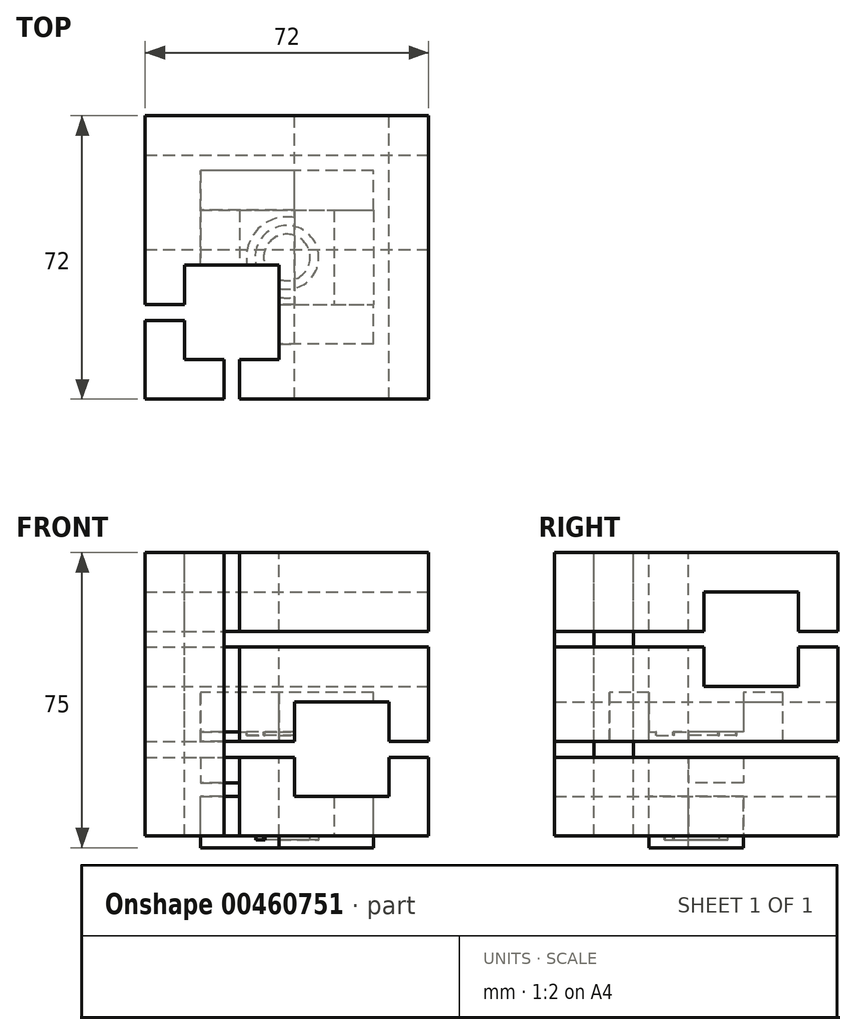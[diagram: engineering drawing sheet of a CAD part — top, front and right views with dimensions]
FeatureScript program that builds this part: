
annotation { "Feature Type Name" : "Feature", "Feature Type Description" : "" }
export const myFeature = defineFeature(function(context is Context, id is Id, definition is map)
    precondition{}
    {
        {
            var Q0;
            Q0=qCreatedBy(makeId("Top.planeOp"),FACE);
            var sketch = newSketch(context, id + "F0", { "sketchPlane" : qUnion([Q0])});
            skLineSegment(sketch, "E0.bottom", {"start": v(12, 12) * mm, "end": v(-12, 12) * mm});
            skLineSegment(sketch, "E0.top", {"start": v(12, -12) * mm, "end": v(-12, -12) * mm});
            skLineSegment(sketch, "E0.left", {"start": v(12, 12) * mm, "end": v(12, -12) * mm});
            skLineSegment(sketch, "E0.right", {"start": v(-12, 12) * mm, "end": v(-12, -12) * mm});
            skPoint(sketch, "E0.middle", {"position": v(0, 0) * mm});
            skLineSegment(sketch, "E1.bottom", {"start": v(12, 12) * mm, "end": v(22, 12) * mm});
            skLineSegment(sketch, "E1.top", {"start": v(12, -12) * mm, "end": v(22, -12) * mm});
            skLineSegment(sketch, "E1.right", {"start": v(22, 12) * mm, "end": v(22, -12) * mm});
            skLineSegment(sketch, "E2.MirrorCS", {"start": v(-12, -12) * mm, "end": v(-22, -12) * mm});
            skLineSegment(sketch, "E3.MirrorCS", {"start": v(-22, 12) * mm, "end": v(-22, -12) * mm});
            skLineSegment(sketch, "E4.MirrorCS", {"start": v(-12, 12) * mm, "end": v(-22, 12) * mm});
            skPoint(sketch, "E5", {"position": v(-17, 0) * mm});
            skPoint(sketch, "E5.positionSnap0", {"position": v(-17, 12) * mm});
            skPoint(sketch, "E5.positionSnap1", {"position": v(-22, 0) * mm});
            skPoint(sketch, "E6", {"position": v(17, 0) * mm});
            skPoint(sketch, "E6.positionSnap0", {"position": v(22, 0) * mm});
            skPoint(sketch, "E6.positionSnap1", {"position": v(17, 12) * mm});
            skCircle(sketch, "E7", {"center": v(0, 0) * mm, "radius": 8.1 * mm});
            skCircle(sketch, "E8", {"center": v(0, 0) * mm, "radius": 5.9 * mm});
            skSolve(sketch);
        }
        {
            var Q0;
            Q0=makeQuery(id+"F0.imprint","IMPRINT",FACE,{"disambiguationData":[TD([[makeQuery(id+"F0.imprint","IMPRINT",EDGE,{"derivedFrom":sQuery(id+"F0.wireOp",EDGE,"E1.bottom")}),-1.0]])]});
            var Q1;
            Q1=makeQuery(id+"F0.imprint","IMPRINT",FACE,{"disambiguationData":[TD([[makeQuery(id+"F0.imprint","IMPRINT",EDGE,{"derivedFrom":sQuery(id+"F0.wireOp",EDGE,"E0.bottom")}),1.0]])]});
            var Q2;
            Q2=makeQuery(id+"F0.imprint","IMPRINT",FACE,{"disambiguationData":[TD([[makeQuery(id+"F0.imprint","IMPRINT",EDGE,{"derivedFrom":sQuery(id+"F0.wireOp",EDGE,"E0.right")}),-1.0]])]});
            var Q3;
            Q3=makeQuery(id+"F0.imprint","IMPRINT",FACE,{"disambiguationData":[TD([[makeQuery(id+"F0.imprint","IMPRINT",EDGE,{"derivedFrom":sQuery(id+"F0.wireOp",EDGE,"E7")}),1.0]])]});
            var Q4;
            Q4=makeQuery(id+"F0.imprint","IMPRINT",FACE,{"disambiguationData":[TD([[makeQuery(id+"F0.imprint","IMPRINT",EDGE,{"derivedFrom":sQuery(id+"F0.wireOp",EDGE,"E8")}),1.0]])]});
            extrude(context, id + "F1", {"entities" : qUnion([Q0, Q1, Q2, Q3, Q4]), "oppositeDirection" : true, "depth" : 3 * mm});
        }
        {
            var Q0;
            Q0=makeQuery(id+"F0.imprint","IMPRINT",FACE,{"disambiguationData":[TD([[makeQuery(id+"F0.imprint","IMPRINT",EDGE,{"derivedFrom":sQuery(id+"F0.wireOp",EDGE,"E1.bottom")}),-1.0]])]});
            var Q1;
            Q1=makeQuery(id+"F0.imprint","IMPRINT",FACE,{"disambiguationData":[TD([[makeQuery(id+"F0.imprint","IMPRINT",EDGE,{"derivedFrom":sQuery(id+"F0.wireOp",EDGE,"E0.right")}),-1.0]])]});
            extrude(context, id + "F2", {"entities" : qUnion([Q0, Q1]), "operationType" : NewBodyOperationType.ADD, "depth" : 10 * mm});
        }
        {
            var Q0;
            Q0=makeQuery(id+"F0.imprint","IMPRINT",FACE,{"disambiguationData":[TD([[makeQuery(id+"F0.imprint","IMPRINT",EDGE,{"derivedFrom":sQuery(id+"F0.wireOp",EDGE,"E7")}),1.0]])]});
            extrude(context, id + "F3", {"entities" : qUnion([Q0]), "operationType" : NewBodyOperationType.REMOVE, "oppositeDirection" : true, "depth" : 1 * mm});
        }
        {
            var Q0;
            Q0=makeQuery(id+"F2.opExtrude","CAP_FACE",FACE,{"disambiguationData":[OSD([sQuery(id+"F0.wireOp",EDGE,"E0.right"),sQuery(id+"F0.wireOp",EDGE,"E2.MirrorCS"),sQuery(id+"F0.wireOp",EDGE,"E3.MirrorCS"),sQuery(id+"F0.wireOp",EDGE,"E4.MirrorCS")])],"isStart":false});
            cPlane(context, id + "F4", {"entities" : qUnion([Q0]), "cplaneType" : CPlaneType.OFFSET, "offset" : 3.5 * mm, "width" : 150 * mm, "height" : 150 * mm});
        }
        {
            var Q0;
            Q0=qCreatedBy(id+"F4.planeOp",FACE);
            var sketch = newSketch(context, id + "F5", { "sketchPlane" : qUnion([Q0])});
            skLineSegment(sketch, "E9.bottom", {"start": v(12, 12) * mm, "end": v(-12, 12) * mm});
            skLineSegment(sketch, "E9.top", {"start": v(12, -12) * mm, "end": v(-12, -12) * mm});
            skLineSegment(sketch, "E9.left", {"start": v(12, 12) * mm, "end": v(12, -12) * mm});
            skLineSegment(sketch, "E9.right", {"start": v(-12, 12) * mm, "end": v(-12, -12) * mm});
            skPoint(sketch, "E9.middle", {"position": v(0, 0) * mm});
            skLineSegment(sketch, "E10.bottom", {"start": v(12, 12) * mm, "end": v(22, 12) * mm});
            skLineSegment(sketch, "E10.top", {"start": v(12, -12) * mm, "end": v(22, -12) * mm});
            skLineSegment(sketch, "E10.right", {"start": v(22, 12) * mm, "end": v(22, -12) * mm});
            skLineSegment(sketch, "E11.MirrorCS", {"start": v(-12, 12) * mm, "end": v(-22, 12) * mm});
            skLineSegment(sketch, "E12.MirrorCS", {"start": v(-22, 12) * mm, "end": v(-22, -12) * mm});
            skLineSegment(sketch, "E13.MirrorCS", {"start": v(-12, -12) * mm, "end": v(-22, -12) * mm});
            skSolve(sketch);
        }
        {
            var Q0;
            Q0=makeQuery(id+"F5.imprint","IMPRINT",FACE,{"disambiguationData":[TD([[makeQuery(id+"F5.imprint","IMPRINT",EDGE,{"derivedFrom":sQuery(id+"F5.wireOp",EDGE,"E9.right")}),-1.0]])]});
            var Q1;
            Q1=makeQuery(id+"F5.imprint","IMPRINT",FACE,{"disambiguationData":[TD([[makeQuery(id+"F5.imprint","IMPRINT",EDGE,{"derivedFrom":sQuery(id+"F5.wireOp",EDGE,"E10.bottom")}),-1.0]])]});
            var Q2;
            Q2=makeQuery(id+"F5.imprint","IMPRINT",FACE,{"disambiguationData":[TD([[makeQuery(id+"F5.imprint","IMPRINT",EDGE,{"derivedFrom":sQuery(id+"F5.wireOp",EDGE,"E9.bottom")}),1.0]])]});
            extrude(context, id + "F6", {"entities" : qUnion([Q0, Q1, Q2]), "depth" : 13 * mm});
        }
        {
            var Q0;
            Q0=makeQuery(id+"F5.imprint","IMPRINT",FACE,{"disambiguationData":[TD([[makeQuery(id+"F5.imprint","IMPRINT",EDGE,{"derivedFrom":sQuery(id+"F5.wireOp",EDGE,"E9.bottom")}),1.0]])]});
            extrude(context, id + "F7", {"entities" : qUnion([Q0]), "operationType" : NewBodyOperationType.REMOVE, "depth" : 10 * mm});
        }
        {
            var Q0;
            Q0=makeQuery(id+"F6.opExtrude","CAP_FACE",FACE,{"disambiguationData":[OSD([sQuery(id+"F5.wireOp",EDGE,"E9.bottom"),sQuery(id+"F5.wireOp",EDGE,"E9.top"),sQuery(id+"F5.wireOp",EDGE,"E10.bottom"),sQuery(id+"F5.wireOp",EDGE,"E10.top"),sQuery(id+"F5.wireOp",EDGE,"E10.right"),sQuery(id+"F5.wireOp",EDGE,"E11.MirrorCS"),sQuery(id+"F5.wireOp",EDGE,"E12.MirrorCS"),sQuery(id+"F5.wireOp",EDGE,"E13.MirrorCS")])],"isStart":false});
            var sketch = newSketch(context, id + "F8", { "sketchPlane" : qUnion([Q0])});
            skLineSegment(sketch, "E14.bottom", {"start": v(22, 22) * mm, "end": v(-22, 22) * mm});
            skLineSegment(sketch, "E14.top", {"start": v(22, -22) * mm, "end": v(-22, -22) * mm});
            skLineSegment(sketch, "E14.left", {"start": v(22, 22) * mm, "end": v(22, -22) * mm});
            skLineSegment(sketch, "E14.right", {"start": v(-22, 22) * mm, "end": v(-22, -22) * mm});
            skPoint(sketch, "E14.middle", {"position": v(0, 0) * mm});
            skLineSegment(sketch, "E15.bottom", {"start": v(22, 12) * mm, "end": v(-22, 12) * mm});
            skLineSegment(sketch, "E15.top", {"start": v(22, -12) * mm, "end": v(-22, -12) * mm});
            skLineSegment(sketch, "E15.left", {"start": v(22, 12) * mm, "end": v(22, -12) * mm});
            skLineSegment(sketch, "E15.right", {"start": v(-22, 12) * mm, "end": v(-22, -12) * mm});
            skPoint(sketch, "E16", {"position": v(0, -17) * mm});
            skPoint(sketch, "E17.MirrorP", {"position": v(0, 17) * mm});
            skCircle(sketch, "E18", {"center": v(0, 0) * mm, "radius": 5.9 * mm});
            skCircle(sketch, "E19.0", {"center": v(0, 0) * mm, "radius": 10.3 * mm});
            skSolve(sketch);
        }
        {
            var Q0;
            {var subQ0=sQuery(id+"F8.wireOp",EDGE,"E14.top");Q0=makeQuery(id+"F8.imprint","IMPRINT",FACE,{"disambiguationData":[TD([[makeQuery(id+"F8.imprint","IMPRINT",EDGE,{"derivedFrom":subQ0}),-1.0]])]});}
            var Q1;
            {var subQ0=sQuery(id+"F8.wireOp",EDGE,"E14.bottom");Q1=makeQuery(id+"F8.imprint","IMPRINT",FACE,{"disambiguationData":[TD([[makeQuery(id+"F8.imprint","IMPRINT",EDGE,{"derivedFrom":subQ0}),1.0]])]});}
            extrude(context, id + "F9", {"entities" : qUnion([Q0, Q1]), "operationType" : NewBodyOperationType.ADD, "oppositeDirection" : true, "depth" : 3 * mm});
        }
        {
            var Q0;
            {var subQ0=sQuery(id+"F8.wireOp",EDGE,"E14.top");Q0=makeQuery(id+"F8.imprint","IMPRINT",FACE,{"disambiguationData":[TD([[makeQuery(id+"F8.imprint","IMPRINT",EDGE,{"derivedFrom":subQ0}),-1.0]])]});}
            var Q1;
            {var subQ0=sQuery(id+"F8.wireOp",EDGE,"E14.bottom");Q1=makeQuery(id+"F8.imprint","IMPRINT",FACE,{"disambiguationData":[TD([[makeQuery(id+"F8.imprint","IMPRINT",EDGE,{"derivedFrom":subQ0}),1.0]])]});}
            extrude(context, id + "F10", {"entities" : qUnion([Q0, Q1]), "operationType" : NewBodyOperationType.ADD, "depth" : 10 * mm});
        }
        {
            var Q0;
            Q0=makeQuery(id+"F8.imprint","IMPRINT",FACE,{"disambiguationData":[TD([[makeQuery(id+"F8.imprint","IMPRINT",EDGE,{"derivedFrom":sQuery(id+"F8.wireOp",EDGE,"E18")}),-1.0]])]});
            extrude(context, id + "F11", {"entities" : qUnion([Q0]), "operationType" : NewBodyOperationType.REMOVE, "oppositeDirection" : true, "depth" : 1 * mm});
        }
        {
            assignVariable(context, id + "F12", {"name" : "LHcubeAs", "anyValue" : 72});
        }
        {
            var Q0;
            Q0=qCreatedBy(makeId("Top.planeOp"),FACE);
            var sketch = newSketch(context, id + "F13", { "sketchPlane" : qUnion([Q0])});
            skLineSegment(sketch, "E20.bottom", {"start": v(36, 36) * mm, "end": v(-36, 36) * mm});
            skLineSegment(sketch, "E20.top", {"start": v(36, -36) * mm, "end": v(-36, -36) * mm});
            skLineSegment(sketch, "E20.left", {"start": v(36, 36) * mm, "end": v(36, -36) * mm});
            skLineSegment(sketch, "E20.right", {"start": v(-36, 36) * mm, "end": v(-36, -36) * mm});
            skPoint(sketch, "E20.middle", {"position": v(0, 0) * mm});
            skSolve(sketch);
        }
        {
            var Q0;
            Q0=makeQuery(id+"F13.imprint","IMPRINT",FACE,{"disambiguationData":[TD([[makeQuery(id+"F13.imprint","IMPRINT",EDGE,{"derivedFrom":sQuery(id+"F13.wireOp",EDGE,"E20.bottom")}),1.0]])]});
            extrude(context, id + "F14", {"entities" : qUnion([Q0]), "depth" : (getVariable(context, 'LHcubeAs')) * mm});
        }
        {
            var Q0;
            Q0=makeQuery(id+"F14.opExtrude","SWEPT_FACE",FACE,{"disambiguationData":[OSD([sQuery(id+"F13.wireOp",EDGE,"E20.bottom")])]});
            var sketch = newSketch(context, id + "F15", { "sketchPlane" : qUnion([Q0])});
            skLineSegment(sketch, "E21.bottom", {"start": v(-26, 10) * mm, "end": v(-2, 10) * mm});
            skLineSegment(sketch, "E21.top", {"start": v(-26, 34) * mm, "end": v(-2, 34) * mm});
            skLineSegment(sketch, "E21.left", {"start": v(-26, 10) * mm, "end": v(-26, 34) * mm});
            skLineSegment(sketch, "E21.right", {"start": v(-2, 10) * mm, "end": v(-2, 34) * mm});
            skPoint(sketch, "E22", {"position": v(-14, 22) * mm});
            skPoint(sketch, "E22.positionSnap0", {"position": v(-2, 22) * mm});
            skPoint(sketch, "E22.positionSnap1", {"position": v(-14, 10) * mm});
            skLineSegment(sketch, "E23.bottom", {"start": v(44.81, 20) * mm, "end": v(-72.81, 20) * mm});
            skLineSegment(sketch, "E23.top", {"start": v(44.81, 24) * mm, "end": v(-72.81, 24) * mm});
            skLineSegment(sketch, "E23.left", {"start": v(44.81, 20) * mm, "end": v(44.81, 24) * mm});
            skLineSegment(sketch, "E23.right", {"start": v(-72.81, 20) * mm, "end": v(-72.81, 24) * mm});
            skLineSegment(sketch, "E24", {"start": v(12, 24) * mm, "end": v(12, 20) * mm});
            skSolve(sketch);
        }
        {
            var Q0;
            Q0=makeQuery(id+"F15.imprint","IMPRINT",FACE,{"disambiguationData":[TD([[makeQuery(id+"F15.imprint","IMPRINT",EDGE,{"derivedFrom":sQuery(id+"F15.wireOp",EDGE,"E21.bottom")}),1.0]])]});
            var Q1;
            {var subQ0=sQuery(id+"F15.wireOp",EDGE,"E21.top");Q1=makeQuery(id+"F15.imprint","IMPRINT",FACE,{"disambiguationData":[TD([[makeQuery(id+"F15.imprint","IMPRINT",EDGE,{"derivedFrom":subQ0}),-1.0]])]});}
            var Q2;
            {var subQ0=sQuery(id+"F15.wireOp",EDGE,"E23.bottom");var subQ1=sQuery(id+"F15.wireOp",EDGE,"E21.left");var subQ2=makeQuery(id+"F15.imprint","INTERSECT",VERTEX,{"derivedFrom":[subQ1,subQ0]});Q2=makeQuery(id+"F15.imprint","IMPRINT",FACE,{"disambiguationData":[TD([[makeQuery(id+"F15.imprint","IMPRINT",EDGE,{"disambiguationData":[TD([[subQ2,-1.0]])],"derivedFrom":subQ1}),1.0]])]});}
            var Q3;
            {var subQ0=sQuery(id+"F15.wireOp",EDGE,"E23.bottom");var subQ1=sQuery(id+"F15.wireOp",EDGE,"E21.left");var subQ2=makeQuery(id+"F15.imprint","INTERSECT",VERTEX,{"derivedFrom":[subQ1,subQ0]});Q3=makeQuery(id+"F15.imprint","IMPRINT",FACE,{"disambiguationData":[TD([[makeQuery(id+"F15.imprint","IMPRINT",EDGE,{"disambiguationData":[TD([[subQ2,-1.0]])],"derivedFrom":subQ1}),-1.0]])]});}
            var Q4;
            {var subQ0=sQuery(id+"F15.wireOp",EDGE,"E23.bottom");var subQ1=sQuery(id+"F15.wireOp",EDGE,"E21.right");var subQ2=makeQuery(id+"F15.imprint","INTERSECT",VERTEX,{"derivedFrom":[subQ1,subQ0]});Q4=makeQuery(id+"F15.imprint","IMPRINT",FACE,{"disambiguationData":[TD([[makeQuery(id+"F15.imprint","IMPRINT",EDGE,{"disambiguationData":[TD([[subQ2,-1.0]])],"derivedFrom":subQ1}),-1.0]])]});}
            extrude(context, id + "F16", {"entities" : qUnion([Q0, Q1, Q2, Q3, Q4]), "operationType" : NewBodyOperationType.REMOVE, "endBound" : BoundingType.THROUGH_ALL, "oppositeDirection" : true, "depth" : 25 * mm});
        }
        {
            var Q0;
            Q0=makeQuery(id+"F14.opExtrude","SWEPT_FACE",FACE,{"disambiguationData":[OSD([sQuery(id+"F13.wireOp",EDGE,"E20.left")])]});
            var sketch = newSketch(context, id + "F17", { "sketchPlane" : qUnion([Q0])});
            skLineSegment(sketch, "E25.bottom", {"start": v(26, 62) * mm, "end": v(2, 62) * mm});
            skLineSegment(sketch, "E25.top", {"start": v(26, 38) * mm, "end": v(2, 38) * mm});
            skLineSegment(sketch, "E25.left", {"start": v(26, 62) * mm, "end": v(26, 38) * mm});
            skLineSegment(sketch, "E25.right", {"start": v(2, 62) * mm, "end": v(2, 38) * mm});
            skPoint(sketch, "E26", {"position": v(14, 50) * mm});
            skPoint(sketch, "E26.positionSnap0", {"position": v(26, 50) * mm});
            skPoint(sketch, "E26.positionSnap1", {"position": v(14, 62) * mm});
            skLineSegment(sketch, "E27.bottom", {"start": v(71.7, 48) * mm, "end": v(-43.7, 48) * mm});
            skLineSegment(sketch, "E27.top", {"start": v(71.7, 52) * mm, "end": v(-43.7, 52) * mm});
            skLineSegment(sketch, "E27.left", {"start": v(71.7, 48) * mm, "end": v(71.7, 52) * mm});
            skLineSegment(sketch, "E27.right", {"start": v(-43.7, 48) * mm, "end": v(-43.7, 52) * mm});
            skLineSegment(sketch, "E28", {"start": v(-12, 52) * mm, "end": v(-12, 48) * mm});
            skSolve(sketch);
        }
        {
            var Q0;
            Q0=makeQuery(id+"F17.imprint","IMPRINT",FACE,{"disambiguationData":[TD([[makeQuery(id+"F17.imprint","IMPRINT",EDGE,{"derivedFrom":sQuery(id+"F17.wireOp",EDGE,"E25.bottom")}),1.0]])]});
            var Q1;
            {var subQ0=sQuery(id+"F17.wireOp",EDGE,"E27.top");var subQ1=sQuery(id+"F17.wireOp",EDGE,"E25.right");var subQ2=makeQuery(id+"F17.imprint","INTERSECT",VERTEX,{"derivedFrom":[subQ1,subQ0]});Q1=makeQuery(id+"F17.imprint","IMPRINT",FACE,{"disambiguationData":[TD([[makeQuery(id+"F17.imprint","IMPRINT",EDGE,{"disambiguationData":[TD([[subQ2,-1.0]])],"derivedFrom":subQ1}),-1.0]])]});}
            var Q2;
            {var subQ0=sQuery(id+"F17.wireOp",EDGE,"E27.top");var subQ1=sQuery(id+"F17.wireOp",EDGE,"E25.left");var subQ2=makeQuery(id+"F17.imprint","INTERSECT",VERTEX,{"derivedFrom":[subQ1,subQ0]});Q2=makeQuery(id+"F17.imprint","IMPRINT",FACE,{"disambiguationData":[TD([[makeQuery(id+"F17.imprint","IMPRINT",EDGE,{"disambiguationData":[TD([[subQ2,-1.0]])],"derivedFrom":subQ1}),-1.0]])]});}
            var Q3;
            {var subQ0=sQuery(id+"F17.wireOp",EDGE,"E25.top");Q3=makeQuery(id+"F17.imprint","IMPRINT",FACE,{"disambiguationData":[TD([[makeQuery(id+"F17.imprint","IMPRINT",EDGE,{"derivedFrom":subQ0}),-1.0]])]});}
            var Q4;
            {var subQ0=sQuery(id+"F17.wireOp",EDGE,"E27.top");var subQ1=sQuery(id+"F17.wireOp",EDGE,"E25.left");var subQ2=makeQuery(id+"F17.imprint","INTERSECT",VERTEX,{"derivedFrom":[subQ1,subQ0]});Q4=makeQuery(id+"F17.imprint","IMPRINT",FACE,{"disambiguationData":[TD([[makeQuery(id+"F17.imprint","IMPRINT",EDGE,{"disambiguationData":[TD([[subQ2,-1.0]])],"derivedFrom":subQ1}),1.0]])]});}
            extrude(context, id + "F18", {"entities" : qUnion([Q0, Q1, Q2, Q3, Q4]), "operationType" : NewBodyOperationType.REMOVE, "endBound" : BoundingType.THROUGH_ALL, "oppositeDirection" : true, "depth" : 25 * mm});
        }
        {
            var Q0;
            Q0=makeQuery(id+"F14.opExtrude","CAP_FACE",FACE,{"disambiguationData":[OSD([sQuery(id+"F13.wireOp",EDGE,"E20.bottom"),sQuery(id+"F13.wireOp",EDGE,"E20.top"),sQuery(id+"F13.wireOp",EDGE,"E20.left"),sQuery(id+"F13.wireOp",EDGE,"E20.right")])],"isStart":false});
            var sketch = newSketch(context, id + "F19", { "sketchPlane" : qUnion([Q0])});
            skLineSegment(sketch, "E29.bottom", {"start": v(-26, -26) * mm, "end": v(-2, -26) * mm});
            skLineSegment(sketch, "E29.top", {"start": v(-26, -2) * mm, "end": v(-2, -2) * mm});
            skLineSegment(sketch, "E29.left", {"start": v(-26, -26) * mm, "end": v(-26, -2) * mm});
            skLineSegment(sketch, "E29.right", {"start": v(-2, -26) * mm, "end": v(-2, -2) * mm});
            skLineSegment(sketch, "E30.bottom", {"start": v(-12, -39.24) * mm, "end": v(-16, -39.24) * mm});
            skLineSegment(sketch, "E30.top", {"start": v(-12, -12.76) * mm, "end": v(-16, -12.76) * mm});
            skLineSegment(sketch, "E30.left", {"start": v(-12, -39.24) * mm, "end": v(-12, -12.76) * mm});
            skLineSegment(sketch, "E30.right", {"start": v(-16, -39.24) * mm, "end": v(-16, -12.76) * mm});
            skPoint(sketch, "E30.middle", {"position": v(-14, -26) * mm});
            skLineSegment(sketch, "E31.bottom", {"start": v(-40.57, -12) * mm, "end": v(-11.43, -12) * mm});
            skLineSegment(sketch, "E31.top", {"start": v(-40.57, -16) * mm, "end": v(-11.43, -16) * mm});
            skLineSegment(sketch, "E31.left", {"start": v(-40.57, -12) * mm, "end": v(-40.57, -16) * mm});
            skLineSegment(sketch, "E31.right", {"start": v(-11.43, -12) * mm, "end": v(-11.43, -16) * mm});
            skPoint(sketch, "E31.middle", {"position": v(-26, -14) * mm});
            skSolve(sketch);
        }
        {
            var Q0;
            Q0=makeQuery(id+"F19.imprint","IMPRINT",FACE,{"disambiguationData":[TD([[makeQuery(id+"F19.imprint","IMPRINT",EDGE,{"derivedFrom":sQuery(id+"F19.wireOp",EDGE,"E29.bottom")}),1.0]])]});
            var Q1;
            {var subQ1=sQuery(id+"F19.wireOp",EDGE,"E29.top");Q1=makeQuery(id+"F19.imprint","IMPRINT",FACE,{"disambiguationData":[TD([[makeQuery(id+"F19.imprint","IMPRINT",EDGE,{"derivedFrom":subQ1}),-1.0]])]});}
            var Q2;
            {var subQ1=sQuery(id+"F19.wireOp",EDGE,"E30.top");Q2=makeQuery(id+"F19.imprint","IMPRINT",FACE,{"disambiguationData":[TD([[makeQuery(id+"F19.imprint","IMPRINT",EDGE,{"derivedFrom":subQ1}),-1.0]])]});}
            var Q3;
            {var subQ0=sQuery(id+"F19.wireOp",EDGE,"E31.top");var subQ1=sQuery(id+"F19.wireOp",EDGE,"E29.left");var subQ2=makeQuery(id+"F19.imprint","INTERSECT",VERTEX,{"derivedFrom":[subQ1,subQ0]});Q3=makeQuery(id+"F19.imprint","IMPRINT",FACE,{"disambiguationData":[TD([[makeQuery(id+"F19.imprint","IMPRINT",EDGE,{"disambiguationData":[TD([[subQ2,-1.0]])],"derivedFrom":subQ1}),1.0]])]});}
            var Q4;
            {var subQ0=sQuery(id+"F19.wireOp",EDGE,"E30.right");var subQ1=sQuery(id+"F19.wireOp",EDGE,"E29.bottom");var subQ2=makeQuery(id+"F19.imprint","INTERSECT",VERTEX,{"derivedFrom":[subQ1,subQ0]});Q4=makeQuery(id+"F19.imprint","IMPRINT",FACE,{"disambiguationData":[TD([[makeQuery(id+"F19.imprint","IMPRINT",EDGE,{"disambiguationData":[TD([[subQ2,-1.0]])],"derivedFrom":subQ1}),-1.0]])]});}
            var Q5;
            {var subQ0=sQuery(id+"F19.wireOp",EDGE,"E30.top");Q5=makeQuery(id+"F19.imprint","IMPRINT",FACE,{"disambiguationData":[TD([[makeQuery(id+"F19.imprint","IMPRINT",EDGE,{"derivedFrom":subQ0}),1.0]])]});}
            extrude(context, id + "F20", {"entities" : qUnion([Q0, Q1, Q2, Q3, Q4, Q5]), "operationType" : NewBodyOperationType.REMOVE, "endBound" : BoundingType.THROUGH_ALL, "oppositeDirection" : true, "depth" : 25 * mm});
        }
        {
            var Q0;
            Q0=makeQuery(id+"F16.boolean.opBoolean","COPY",FACE,{"derivedFrom":makeQuery(id+"F16.opExtrude","SWEPT_FACE",FACE,{"disambiguationData":[OSD([sQuery(id+"F15.wireOp",EDGE,"E24")])]})});
            extrude(context, id + "F21", {"entities" : qUnion([Q0]), "operationType" : NewBodyOperationType.REMOVE, "endBound" : BoundingType.THROUGH_ALL, "oppositeDirection" : true, "depth" : 25 * mm});
        }
        {
            var Q0;
            Q0=makeQuery(id+"F18.boolean.opBoolean","COPY",FACE,{"derivedFrom":makeQuery(id+"F18.opExtrude","SWEPT_FACE",FACE,{"disambiguationData":[OSD([sQuery(id+"F17.wireOp",EDGE,"E28")])]})});
            extrude(context, id + "F22", {"entities" : qUnion([Q0]), "operationType" : NewBodyOperationType.REMOVE, "endBound" : BoundingType.THROUGH_ALL, "oppositeDirection" : true, "depth" : 25 * mm});
        }
        {
            var Q0;
            Q0=makeQuery(id+"F22.boolean.opBoolean","COPY",FACE,{"derivedFrom":makeQuery(id+"F22.opExtrude","SWEPT_FACE",FACE,{"disambiguationData":[OSD([sQuery(id+"F17.wireOp",EDGE,"E28"),sQuery(id+"F19.wireOp",EDGE,"E29.right")])]})});
            extrude(context, id + "F23", {"entities" : qUnion([Q0]), "operationType" : NewBodyOperationType.REMOVE, "endBound" : BoundingType.UP_TO_NEXT, "oppositeDirection" : true, "depth" : 25 * mm});
        }
        {
            var Q0;
            Q0=makeQuery(id+"F21.boolean.opBoolean","COPY",FACE,{"derivedFrom":makeQuery(id+"F21.opExtrude","SWEPT_FACE",FACE,{"disambiguationData":[OSD([sQuery(id+"F15.wireOp",EDGE,"E24"),sQuery(id+"F19.wireOp",EDGE,"E29.top")])]})});
            extrude(context, id + "F24", {"entities" : qUnion([Q0]), "operationType" : NewBodyOperationType.REMOVE, "endBound" : BoundingType.UP_TO_NEXT, "oppositeDirection" : true, "depth" : 25 * mm});
        }
    });
